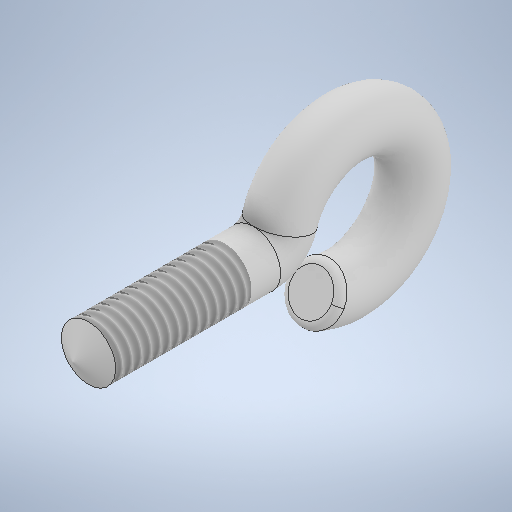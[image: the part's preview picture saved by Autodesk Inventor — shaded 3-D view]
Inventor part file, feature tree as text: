
AUTODESK INVENTOR PART (.ipt)
format: ipt  version: 2025 (Build 290162000, 162)  size: 338,944 bytes
history: native  units: mm
features: sketch x3, sweep x1, revolve x1, thread x1, fillet x1
ambient origin geometry x8: Origin, YZ Plane, XZ Plane, XY Plane, X Axis, Y Axis, Z Axis, Center Point
bodies: Solid1 (feature_tree)
feature tree (7):
  sweep  "Sweep1"
  revolve  "Revolution1"  [1 undecoded]
  thread  "Thread1"  [1 undecoded]
  fillet  "Fillet1"  Radius=4.0mm
  sketch  "Sketch1"  dims[d0=15.0mm d1=90.0deg]
  sketch  "Sketch2"  dims[d2=60.0deg d3=5.0mm d4=2.0mm d5=4.0mm]
  sketch  "Sketch3"  dims[d6=0.0mm d7=0.0mm d8=30.0deg d9=90.0deg d10=10.0mm d11=0.0mm d12=0.5mm]
note: 2 required parameter values undecoded (feature->parameter linkage not recoverable at this tier; creation-order binding heuristic only, values carry confidence <= 0.55)